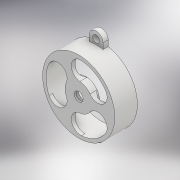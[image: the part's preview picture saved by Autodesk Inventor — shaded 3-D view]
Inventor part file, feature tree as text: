
AUTODESK INVENTOR PART (.ipt)
format: ipt  version: 2018.2 (Build 222227000, 227)  size: 219,136 bytes
history: native  units: mm
features: extrude x6, sketch x3, pattern_circular x1, fillet x1, projected_geometry x1
ambient origin geometry x8: Origin, YZ Plane, XZ Plane, XY Plane, X Axis, Y Axis, Z Axis, Center Point
bodies: Solid1 (feature_tree)
feature tree (12):
  sketch  "Sketch1"  dims[d0=42.0mm d1=2.0mm]
  extrude  "Extrusion1"  Depth=2.0mm
  extrude  "Extrusion5"  Depth=5.175mm
  extrude  "Extrusion6"  Depth=2.0mm TaperAngle=0.0deg
  extrude  "Extrusion2"  Depth=8.0mm
  pattern_circular  "Circular Pattern1"  [2 undecoded]
  extrude  "Extrusion3"  Depth=2.0mm TaperAngle=360.0deg
  extrude  "Extrusion4"  Depth=2.0mm TaperAngle=0.0deg
  fillet  "Fillet1"  Radius=48.0mm
  sketch  "Sketch2"  dims[d2=9.8mm d3=5.175mm]
  sketch  "Sketch3"  dims[d4=8.726646mm d5=1.15mm d6=0.0mm d7=8.0mm d8=3.0mm d9=0.0mm d10=30.0mm d11=360.0deg d13=11.0mm d14=0.0mm d15=48.0mm d16=4.0mm d17=4.0mm d18=3.0mm d19=0.0mm d20=1.0mm d21=0.0mm d22=2.0mm d23=0.0mm d24=2.0mm]
  projected_geometry  "Projected Loop1"
note: 2 required parameter values undecoded (feature->parameter linkage not recoverable at this tier; creation-order binding heuristic only, values carry confidence <= 0.55)
